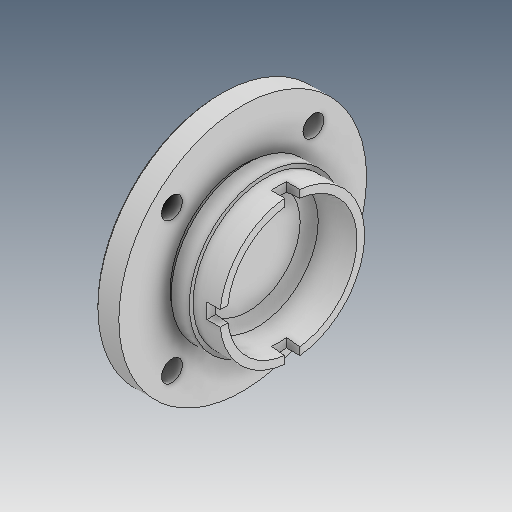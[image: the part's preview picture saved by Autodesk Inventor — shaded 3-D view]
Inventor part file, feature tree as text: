
AUTODESK INVENTOR PART (.ipt)
format: ipt  version: 2025 (Build 290162000, 162)  size: 403,968 bytes
history: native  units: in
note: dims shown in document units (in); Inventor stores cm internally (conversion verified against a paired STEP export)
features: sketch x5, extrude x3, revolve x1, chamfer x1, fillet x1
ambient origin geometry x8: Origin, YZ Plane, XZ Plane, XY Plane, X Axis, Y Axis, Z Axis, Center Point
bodies: 实体1 (feature_tree)
feature tree (11):
  revolve  "旋转1"  [1 undecoded]
  extrude  "拉伸1"  Depth=0.4724in
  extrude  "拉伸2"  Depth=1.4961in
  extrude  "拉伸3"  Depth=0.0984in
  chamfer  "倒角1"  Angle=45.0deg  [1 undecoded]
  fillet  "圆角1"  Radius=0.0394in
  sketch  "草图1"  dims[d3=0.3937in d0=0.4331in d1=1.811in d2=2.5591in]
  sketch  "草图2"  dims[d6=1.5748in d7=1.4961in]
  sketch  "草图3"  dims[d8=0.4724in d9=0.0984in]
  sketch  "草图4"  dims[d10=1.4961in d11=45.0deg d12=0.0394in d13=0.5906in d14=1.3386in d15=0.5792in d16=90.0deg d17=0.2756in d18=0.315in d19=0.0in d20=0.2756in d21=0.315in d22=0.0in d23=0.4331in d24=2.0669in d25=1.5748in d27=360.0deg d29=0.315in d30=0.0in d31=0.0394in d32=0.0787in d33=45.0deg d34=0.1969in d35=45.0deg]
  sketch  "草图 - 环形阵列1"  dims[d4=1.0236in d5=0.4724in]
note: 2 required parameter values undecoded (feature->parameter linkage not recoverable at this tier; creation-order binding heuristic only, values carry confidence <= 0.55)